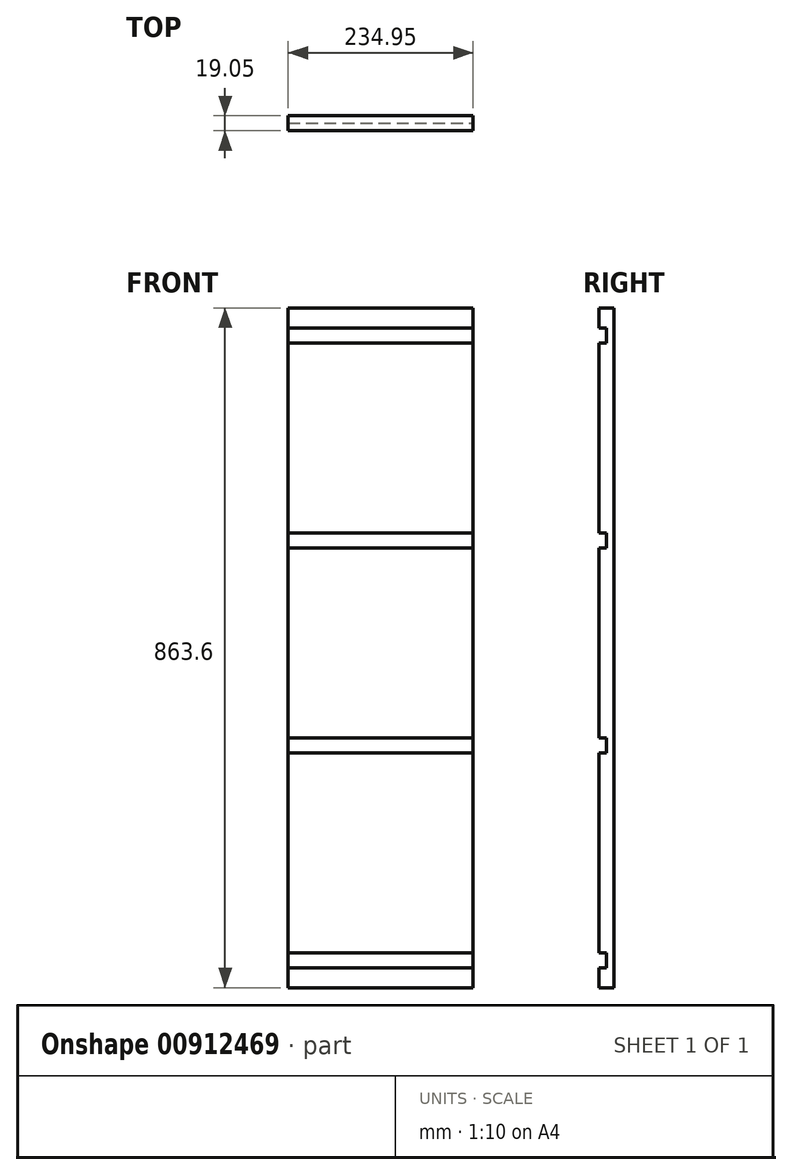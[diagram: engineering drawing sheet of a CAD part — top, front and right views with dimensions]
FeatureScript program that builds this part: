
annotation { "Feature Type Name" : "Feature", "Feature Type Description" : "" }
export const myFeature = defineFeature(function(context is Context, id is Id, definition is map)
    precondition{}
    {
        {
            var Q0;
            Q0=qCreatedBy(makeId("Top.planeOp"),FACE);
            var sketch = newSketch(context, id + "F0", { "sketchPlane" : qUnion([Q0])});
            skLineSegment(sketch, "E0.bottom", {"start": v(0, 0) * mm, "end": v(234.95, 0) * mm});
            skLineSegment(sketch, "E0.top", {"start": v(0, 19.05) * mm, "end": v(234.95, 19.05) * mm});
            skLineSegment(sketch, "E0.left", {"start": v(0, 0) * mm, "end": v(0, 19.05) * mm});
            skLineSegment(sketch, "E0.right", {"start": v(234.95, 0) * mm, "end": v(234.95, 19.05) * mm});
            skSolve(sketch);
        }
        {
            var Q0;
            Q0 = qSketchRegion(id + "F0", true);
            extrude(context, id + "F1", {"entities" : qUnion([Q0]), "depth" : 863.6 * mm, "offsetDistance" : 25.4 * mm});
        }
        {
            var Q0;
            Q0=makeQuery(id+"F1.opExtrude","SWEPT_FACE",FACE,{"disambiguationData":[OSD([sQuery(id+"F0.wireOp",EDGE,"E0.bottom")])]});
            var sketch = newSketch(context, id + "F2", { "sketchPlane" : qUnion([Q0])});
            skLineSegment(sketch, "E1.bottom", {"start": v(0, 838.2) * mm, "end": v(234.95, 838.2) * mm});
            skLineSegment(sketch, "E1.top", {"start": v(0, 819.15) * mm, "end": v(234.95, 819.15) * mm});
            skLineSegment(sketch, "E1.left", {"start": v(0, 838.2) * mm, "end": v(0, 819.15) * mm});
            skLineSegment(sketch, "E1.right", {"start": v(234.95, 838.2) * mm, "end": v(234.95, 819.15) * mm});
            skLineSegment(sketch, "E2.bottom", {"start": v(234.95, 25.4) * mm, "end": v(0, 25.4) * mm});
            skLineSegment(sketch, "E2.top", {"start": v(234.95, 44.45) * mm, "end": v(0, 44.45) * mm});
            skLineSegment(sketch, "E2.left", {"start": v(234.95, 25.4) * mm, "end": v(234.95, 44.45) * mm});
            skLineSegment(sketch, "E2.right", {"start": v(0, 25.4) * mm, "end": v(0, 44.45) * mm});
            skLineSegment(sketch, "E3.bottom", {"start": v(0, 317.5) * mm, "end": v(234.95, 317.5) * mm});
            skLineSegment(sketch, "E3.top", {"start": v(0, 298.45) * mm, "end": v(234.95, 298.45) * mm});
            skLineSegment(sketch, "E3.left", {"start": v(0, 317.5) * mm, "end": v(0, 298.45) * mm});
            skLineSegment(sketch, "E3.right", {"start": v(234.95, 317.5) * mm, "end": v(234.95, 298.45) * mm});
            skLineSegment(sketch, "E4.bottom", {"start": v(0, 577.85) * mm, "end": v(234.95, 577.85) * mm});
            skLineSegment(sketch, "E4.top", {"start": v(0, 558.8) * mm, "end": v(234.95, 558.8) * mm});
            skLineSegment(sketch, "E4.left", {"start": v(0, 577.85) * mm, "end": v(0, 558.8) * mm});
            skLineSegment(sketch, "E4.right", {"start": v(234.95, 577.85) * mm, "end": v(234.95, 558.8) * mm});
            skSolve(sketch);
        }
        {
            var Q0;
            Q0 = qSketchRegion(id + "F2", true);
            extrude(context, id + "F3", {"entities" : qUnion([Q0]), "operationType" : NewBodyOperationType.REMOVE, "oppositeDirection" : true, "depth" : 9.52 * mm, "offsetDistance" : 25.4 * mm});
        }
    });
